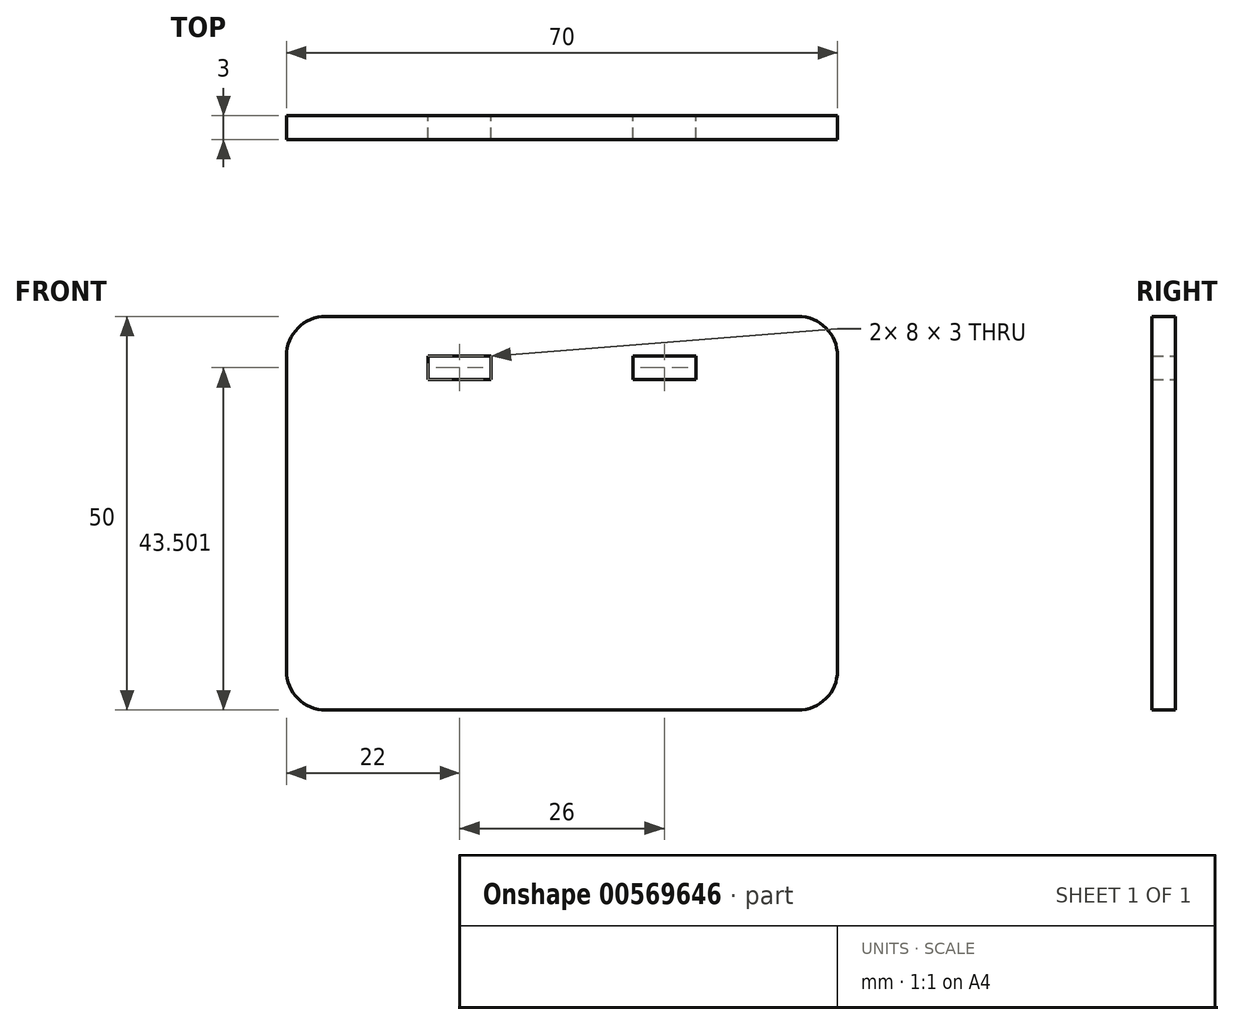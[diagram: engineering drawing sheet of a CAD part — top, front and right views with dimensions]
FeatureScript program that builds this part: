
annotation { "Feature Type Name" : "Feature", "Feature Type Description" : "" }
export const myFeature = defineFeature(function(context is Context, id is Id, definition is map)
    precondition{}
    {
        {
            var Q0;
            Q0=qCreatedBy(makeId("Front.planeOp"),FACE);
            var sketch = newSketch(context, id + "F0", { "sketchPlane" : qUnion([Q0])});
            skLineSegment(sketch, "E0.bottom", {"start": v(-30, 26.57) * mm, "end": v(30, 26.57) * mm});
            skLineSegment(sketch, "E0.top", {"start": v(-30, -23.43) * mm, "end": v(30, -23.43) * mm});
            skLineSegment(sketch, "E0.left", {"start": v(-35, 21.57) * mm, "end": v(-35, -18.43) * mm});
            skLineSegment(sketch, "E0.right", {"start": v(35, 21.57) * mm, "end": v(35, -18.43) * mm});
            skLineSegment(sketch, "E1", {"start": v(-58.85, 21.57) * mm, "end": v(51.4, 21.57) * mm, "construction": true});
            skLineSegment(sketch, "E2", {"start": v(-60.98, 18.57) * mm, "end": v(51.4, 18.57) * mm, "construction": true});
            skLineSegment(sketch, "E3.bottom", {"start": v(-17, 21.57) * mm, "end": v(-9, 21.57) * mm});
            skLineSegment(sketch, "E3.top", {"start": v(-17, 18.57) * mm, "end": v(-9, 18.57) * mm});
            skLineSegment(sketch, "E3.left", {"start": v(-17, 21.57) * mm, "end": v(-17, 18.57) * mm});
            skLineSegment(sketch, "E3.right", {"start": v(-9, 21.57) * mm, "end": v(-9, 18.57) * mm});
            skLineSegment(sketch, "E4.bottom", {"start": v(9, 21.57) * mm, "end": v(17, 21.57) * mm});
            skLineSegment(sketch, "E4.top", {"start": v(9, 18.57) * mm, "end": v(17, 18.57) * mm});
            skLineSegment(sketch, "E4.left", {"start": v(9, 21.57) * mm, "end": v(9, 18.57) * mm});
            skLineSegment(sketch, "E4.right", {"start": v(17, 21.57) * mm, "end": v(17, 18.57) * mm});
            skPoint(sketch, "E5.visualSharp", {"position": v(35, 26.57) * mm});
            skArc(sketch, "E5.filletArc", {"start": v(35, 21.57) * mm, "mid": v(33.54, 25.1) * mm, "end": v(30, 26.57) * mm});
            skPoint(sketch, "E6.visualSharp", {"position": v(-35, 26.57) * mm});
            skArc(sketch, "E6.filletArc", {"start": v(-30, 26.57) * mm, "mid": v(-33.54, 25.1) * mm, "end": v(-35, 21.57) * mm});
            skPoint(sketch, "E7.visualSharp", {"position": v(-35, -23.43) * mm});
            skArc(sketch, "E7.filletArc", {"start": v(-35, -18.43) * mm, "mid": v(-33.54, -21.96) * mm, "end": v(-30, -23.43) * mm});
            skPoint(sketch, "E8.visualSharp", {"position": v(35, -23.43) * mm});
            skArc(sketch, "E8.filletArc", {"start": v(30, -23.43) * mm, "mid": v(33.54, -21.96) * mm, "end": v(35, -18.43) * mm});
            skSolve(sketch);
        }
        {
            var Q0;
            Q0=makeQuery(id+"F0.imprint","IMPRINT",FACE,{"disambiguationData":[TD([[makeQuery(id+"F0.imprint","IMPRINT",EDGE,{"derivedFrom":sQuery(id+"F0.wireOp",EDGE,"E0.bottom")}),-1.0]])]});
            var Q1;
            Q1 = qSketchRegion(id + "F0", true);
            extrude(context, id + "F1", {"entities" : qUnion([Q0, Q1]), "depth" : 3 * mm, "offsetDistance" : 25 * mm});
        }
    });
